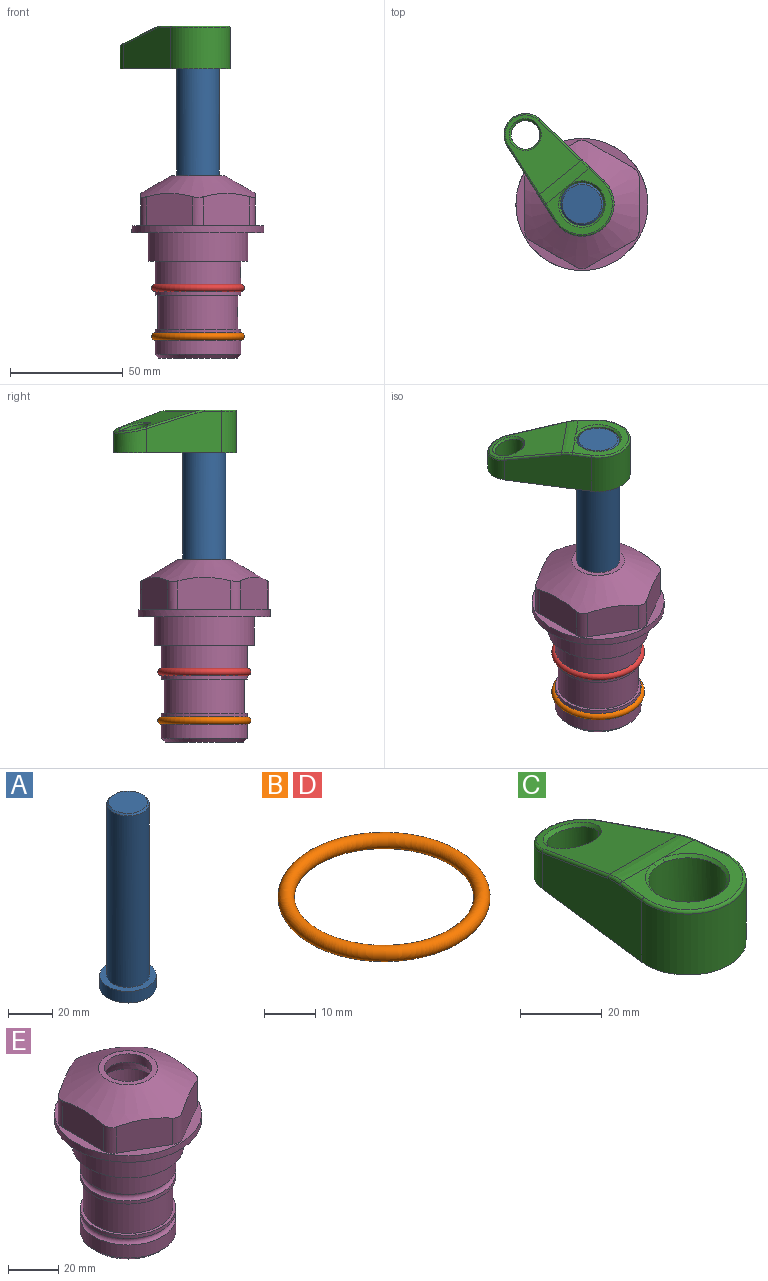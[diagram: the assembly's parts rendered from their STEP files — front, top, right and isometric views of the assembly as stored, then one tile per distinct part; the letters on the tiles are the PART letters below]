
ASSEMBLY  parts=5 mates=4
PART A: 6 faces, bbox 25.4x25.4x101.6 mm
  f0: plane 17.46x17.46mm, normal (0,0,1), area 239.5mm2, adj f5
  f1: plane 25.4x25.4mm, normal (0,0,-1), area 506.7mm2, adj f2
  f2: cylinder r=12.7mm len=25.4mm, axis (0,0,1), area 506.7mm2, adj f1,f3
  f3: plane 25.4x25.4mm, normal (0,0,1), area 221.7mm2, adj f2,f4
  f4: cylinder r=9.53mm len=94.46mm, axis (0,0,1), area 5653mm2, adj f3,f5
  f5: cone r=8.73mm half-angle=45deg, axis (0,0,-1), area 64.4mm2, adj f0,f4
PART B: 1 faces, bbox 44.7x44.7x3.2 mm
  f0: torus R=19.05mm, axis (0,0,1), area 1193.9mm2
PART C: 31 faces, bbox 31.7x65.5x19.8 mm
  f0: plane 39.12x18.26mm, normal (0.99,0.12,0), area 612.2mm2, adj f1,f4,f7,f11,f13,f15
  f1: cylinder r=9.53mm len=18.91mm, axis (0,0,-1), area 296.1mm2, adj f0,f2,f7,f17
  f2: plane 39.12x18.26mm, normal (-0.99,0.12,0), area 612.2mm2, adj f1,f4,f7,f12,f14,f16
  f3: cylinder r=6.35mm len=12.7mm, axis (0,0,-1), area 362.4mm2, adj f7,f18
  f4: cylinder r=14.29mm len=28.58mm, axis (0,0,-1), area 882.2mm2, adj f0,f2,f7,f10
  f5: cylinder r=9.53mm len=19.05mm, axis (0,0,-1), area 1092.6mm2, adj f7,f19,f20
  f6: plane 26.99x23.69mm, normal (0,0,1), area 216.2mm2, adj f9,f10,f11,f12,f19
  f7: plane 63.5x28.58mm, normal (0,0,-1), area 661.8mm2, adj f0,f1,f2,f3,f4,f5,f22,f23
  f8: plane 33.52x23.6mm, normal (0,0.26,0.97), area 486mm2, adj f9,f15,f16,f17,f18
  f9: cylinder r=19.05mm len=24.72mm, axis (1,0,0), area 120.4mm2, adj f6,f8,f13,f14,f20
  f10: torus R=13.49mm, axis (0,0,1), area 59mm2, adj f4,f6,f11,f12
  f11: cylinder r=0.79mm len=8.67mm, axis (0.12,-0.99,0), area 10.8mm2, adj f0,f6,f10,f13
  f12: cylinder r=0.79mm len=8.67mm, axis (0.12,0.99,0), area 10.8mm2, adj f2,f6,f10,f14
  f13: bspline ~4.95x1.42mm, area 6.1mm2, adj f0,f9,f11,f15
  f14: bspline ~4.95x1.42mm, area 6.1mm2, adj f2,f9,f12,f16
  f15: cylinder r=0.79mm len=25.95mm, axis (0.12,-0.96,0.26), area 32.9mm2, adj f0,f8,f13,f17
  f16: cylinder r=0.79mm len=25.95mm, axis (0.12,0.96,-0.26), area 32.9mm2, adj f2,f8,f14,f17
  f17: bspline ~18.91x8.38mm, area 30mm2, adj f1,f8,f15,f16
  f18: bspline ~14.29x14.29mm, area 48.3mm2, adj f3,f8
  f19: cone r=9.53mm half-angle=45deg, axis (0,0,1), area 66.5mm2, adj f5,f6,f20
  f20: bspline ~3.22x0.96mm, area 3.5mm2, adj f5,f9,f19
  f21: plane 2.75x2.72mm, normal (0,0,-1), area 2.9mm2, adj f23,f25,f28
  f22: plane 23.05x15.88mm, normal (-0.99,-0.12,0), area 323.6mm2, adj f7,f25,f26,f27,f28,f29
  f23: plane 23.05x15.88mm, normal (0.99,-0.12,0), area 323.6mm2, adj f7,f21,f25,f27,f28,f30
  f24: cylinder r=9.53mm len=10.69mm, axis (0,0,-1), area 114.7mm2, adj f7,f27,f29,f30
  f25: cylinder r=12.7mm len=20.59mm, axis (0,0,-1), area 381.1mm2, adj f7,f21,f22,f23,f26,f28
  f26: plane 2.75x2.72mm, normal (0,0,-1), area 2.9mm2, adj f22,f25,f28
  f27: plane 19.72x18.37mm, normal (0,-0.26,-0.97), area 291.8mm2, adj f22,f23,f24,f28,f29,f30
  f28: cylinder r=15.88mm len=19.92mm, axis (1,0,0), area 54.8mm2, adj f21,f22,f23,f25,f26,f27
  f29: cylinder r=1.59mm len=11mm, axis (0,0,-1), area 34.7mm2, adj f7,f22,f24,f27
  f30: cylinder r=1.59mm len=11mm, axis (0,0,-1), area 34.7mm2, adj f7,f23,f24,f27
PART D: same geometry as B
PART E: 36 faces, bbox 58.7x58.7x81 mm
  f0: cylinder r=17.78mm len=35.56mm, axis (0,0,1), area 1670.8mm2, adj f23,f24,f31
  f1: cylinder r=19.05mm len=38.1mm, axis (0,0,1), area 1191.9mm2, adj f26,f27,f30
  f2: plane 58.66x58.66mm, normal (0,0,-1), area 1150.6mm2, adj f3,f28
  f3: cylinder r=29.33mm len=58.66mm, axis (0,0,-1), area 585.1mm2, adj f2,f4
  f4: plane 58.66x58.66mm, normal (0,0,1), area 475.9mm2, adj f3,f5,f6,f7,f8,f9,f10,f11
  f5: plane 20.32x14.34mm, normal (-0.5,0.87,0), area 324.4mm2, adj f4,f15,f16,f17
  f6: plane 20.32x14.34mm, normal (0.5,0.87,0), area 324.4mm2, adj f4,f14,f15,f17
  f7: plane 23.48x14.34mm, normal (1,0,0), area 324.4mm2, adj f4,f13,f14,f17
  f8: plane 20.32x14.34mm, normal (0.5,-0.87,0), area 324.4mm2, adj f4,f12,f13,f17
  f9: plane 20.32x14.34mm, normal (-0.5,-0.87,0), area 324.4mm2, adj f4,f11,f12,f17
  f10: plane 23.48x14.34mm, normal (-1,0,0), area 324.4mm2, adj f4,f11,f16,f17
  f11: cylinder r=5.08mm len=12.85mm, axis (0,0,-1), area 67.2mm2, adj f4,f9,f10,f17
  f12: cylinder r=5.08mm len=12.85mm, axis (0,0,-1), area 67.2mm2, adj f4,f8,f9,f17
  f13: cylinder r=5.08mm len=12.85mm, axis (0,0,-1), area 67.2mm2, adj f4,f7,f8,f17
  f14: cylinder r=5.08mm len=12.85mm, axis (0,0,-1), area 67.2mm2, adj f4,f6,f7,f17
  f15: cylinder r=5.08mm len=12.85mm, axis (0,0,-1), area 67.2mm2, adj f4,f5,f6,f17
  f16: cylinder r=5.08mm len=12.85mm, axis (0,0,-1), area 67.2mm2, adj f4,f5,f10,f17
  f17: cone r=11.73mm half-angle=60deg, axis (0,0,-1), area 2071.8mm2, adj f5,f6,f7,f8,f9,f10,f11,f12
  f18: plane 23.46x23.46mm, normal (0,0,1), area 147.4mm2, adj f17,f35
  f19: plane 34.93x34.93mm, normal (0,0,-1), area 958mm2, adj f29
  f20: cylinder r=19.05mm len=38.1mm, axis (0,0,1), area 760.1mm2, adj f21,f29
  f21: torus R=19.05mm, axis (0,0,1), area 565.3mm2, adj f20,f22
  f22: cylinder r=19.05mm len=38.1mm, axis (0,0,1), area 190mm2, adj f21,f23
  f23: plane 38.1x38.1mm, normal (0,0,1), area 146.9mm2, adj f0,f22
  f24: plane 38.1x38.1mm, normal (0,0,-1), area 146.9mm2, adj f0,f25
  f25: cylinder r=19.05mm len=38.1mm, axis (0,0,1), area 190mm2, adj f24,f26
  f26: torus R=19.05mm, axis (0,0,1), area 565.3mm2, adj f1,f25
  f27: plane 44.45x44.45mm, normal (0,0,-1), area 411.7mm2, adj f1,f28
  f28: cylinder r=22.23mm len=44.45mm, axis (0,0,1), area 1773.5mm2, adj f2,f27
  f29: cone r=19.05mm half-angle=45deg, axis (0,0,1), area 257.5mm2, adj f19,f20
  f30: cylinder r=3.17mm len=6.75mm, axis (-1,0,0), area 128mm2, adj f1,f33
  f31: cylinder r=3.17mm len=6.35mm, axis (-1,0,0), area 102.5mm2, adj f0,f33
  f32: plane 25.4x25.4mm, normal (0,0,1), area 506.7mm2, adj f33
  f33: cylinder r=12.7mm len=66.42mm, axis (0,0,-1), area 5236.2mm2, adj f30,f31,f32,f34
  f34: cone r=9.53mm half-angle=30deg, axis (0,0,-1), area 443.4mm2, adj f33,f35
  f35: cylinder r=9.53mm len=19.05mm, axis (0,0,-1), area 240.9mm2, adj f18,f34
PLACE A rot(axis=(0,0,1),39.2deg) t=(0,0,27.55)mm
PLACE B t=(0,0,-21.59)mm
PLACE C rot(axis=(0,0,1),39.2deg) t=(0,0,28.35)mm
PLACE D at identity
PLACE E at identity fixed
MATE cylindrical E.f0 <-> A.f2  axis (0,0,1) through (0,0,-50.55)mm
MATE fastened A.f2 <-> C.f4  axis (0,0,1) through (0,0,91.05)mm
MATE fastened E.f0 <-> B.f0  axis (0,0,1) through (0,0,-46.1)mm
MATE fastened E.f0 <-> D.f0  axis (0,0,1) through (0,0,-24.51)mm
